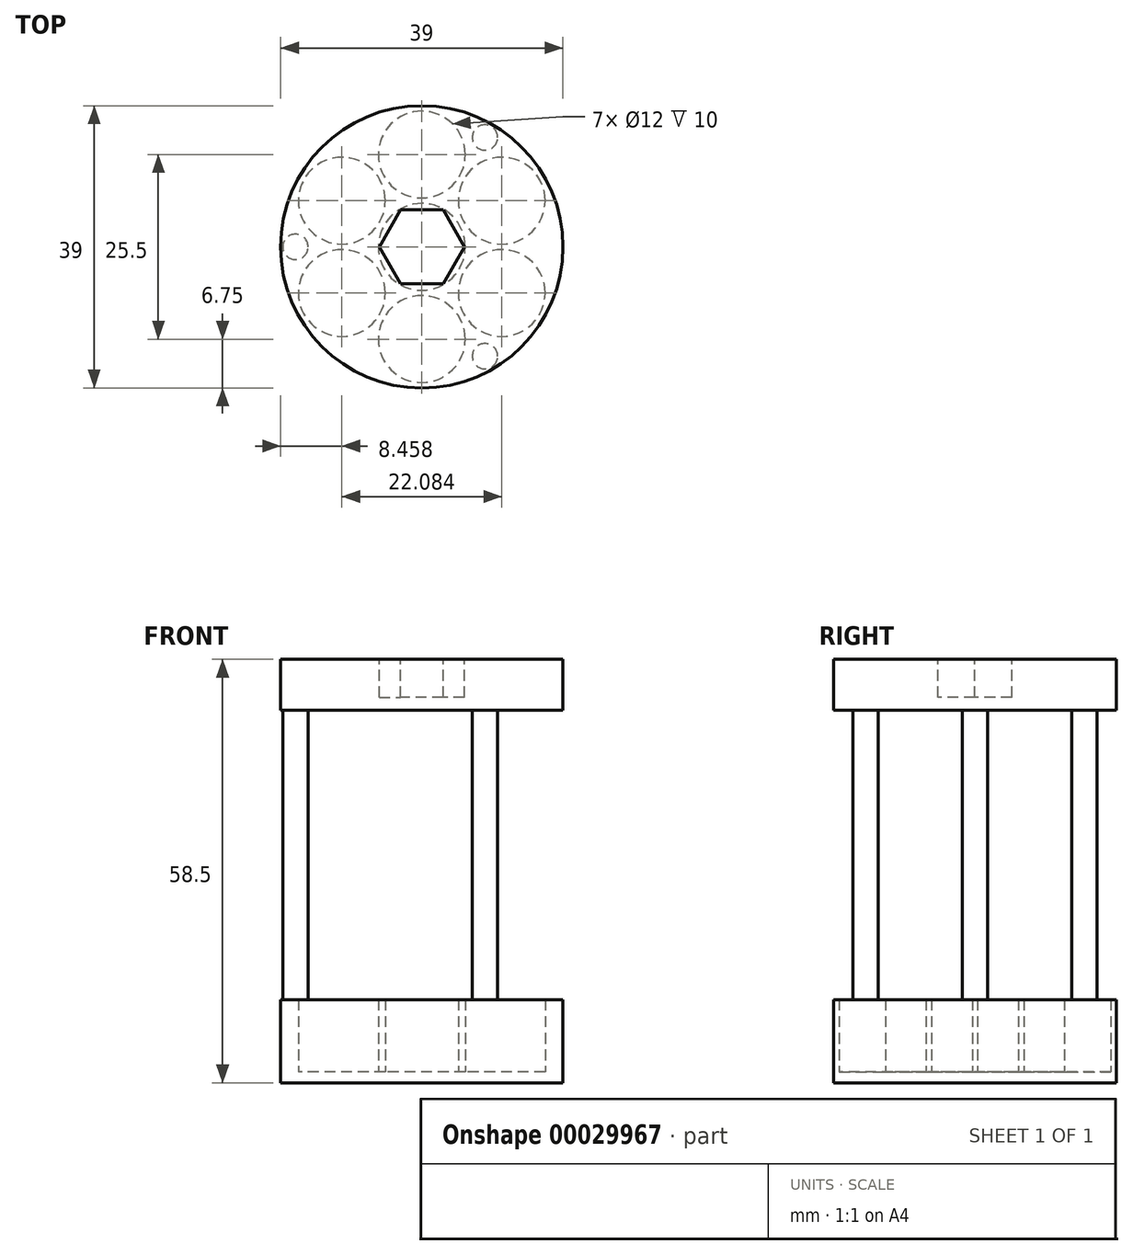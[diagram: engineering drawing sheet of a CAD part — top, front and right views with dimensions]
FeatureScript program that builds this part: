
annotation { "Feature Type Name" : "Feature", "Feature Type Description" : "" }
export const myFeature = defineFeature(function(context is Context, id is Id, definition is map)
    precondition{}
    {
        {
            var Q0;
            Q0=qCreatedBy(makeId("Top.planeOp"),FACE);
            var sketch = newSketch(context, id + "F0", { "sketchPlane" : qUnion([Q0])});
            skCircle(sketch, "E0", {"center": v(0, 0) * mm, "radius": 19.5 * mm});
            skSolve(sketch);
        }
        {
            var Q0;
            Q0=qSketchRegion(id+"F0",true);
            extrude(context, id + "F1", {"entities" : qUnion([Q0]), "depth" : 1.5 * mm});
        }
        {
            var Q0;
            Q0=makeQuery(id+"F1.opExtrude","CAP_FACE",FACE,{"disambiguationData":[OSD([sQuery(id+"F0.wireOp",EDGE,"E0")])],"isStart":false});
            var sketch = newSketch(context, id + "F2", { "sketchPlane" : qUnion([Q0])});
            skCircle(sketch, "E1", {"center": v(0, 0) * mm, "radius": 19.5 * mm});
            skCircle(sketch, "E2", {"center": v(0, 0) * mm, "radius": 6 * mm});
            skLineSegment(sketch, "E3", {"start": v(0, 6) * mm, "end": v(0, 19.5) * mm});
            skCircle(sketch, "E4", {"center": v(0, 12.75) * mm, "radius": 6 * mm});
            skCircle(sketch, "E5.1.0", {"center": v(-11.04, 6.38) * mm, "radius": 6 * mm});
            skCircle(sketch, "E5.2.0", {"center": v(-11.04, -6.37) * mm, "radius": 6 * mm});
            skCircle(sketch, "E5.3.0", {"center": v(0, -12.75) * mm, "radius": 6 * mm});
            skCircle(sketch, "E5.4.0", {"center": v(11.04, -6.38) * mm, "radius": 6 * mm});
            skCircle(sketch, "E5.5.0", {"center": v(11.04, 6.38) * mm, "radius": 6 * mm});
            skSolve(sketch);
        }
        {
            var Q0;
            Q0=makeQuery(id+"F2.imprint","IMPRINT",FACE,{"disambiguationData":[TD([[makeQuery(id+"F2.imprint","IMPRINT",EDGE,{"derivedFrom":sQuery(id+"F2.wireOp",EDGE,"E1")}),1.0]])]});
            extrude(context, id + "F3", {"entities" : qUnion([Q0]), "operationType" : NewBodyOperationType.ADD, "depth" : 10 * mm});
        }
        {
            var Q0;
            Q0=makeQuery(id+"F3.opExtrude","CAP_FACE",FACE,{"disambiguationData":[OSD([sQuery(id+"F2.wireOp",EDGE,"E1"),sQuery(id+"F2.wireOp",EDGE,"E2"),sQuery(id+"F2.wireOp",EDGE,"E4"),sQuery(id+"F2.wireOp",EDGE,"E5.1.0"),sQuery(id+"F2.wireOp",EDGE,"E5.2.0"),sQuery(id+"F2.wireOp",EDGE,"E5.3.0"),sQuery(id+"F2.wireOp",EDGE,"E5.4.0"),sQuery(id+"F2.wireOp",EDGE,"E5.5.0")])],"isStart":false});
            var sketch = newSketch(context, id + "F4", { "sketchPlane" : qUnion([Q0])});
            skCircle(sketch, "E6", {"center": v(-17.45, 0) * mm, "radius": 1.75 * mm});
            skCircle(sketch, "E7.1.0", {"center": v(8.72, -15.11) * mm, "radius": 1.75 * mm});
            skCircle(sketch, "E7.2.0", {"center": v(8.72, 15.11) * mm, "radius": 1.75 * mm});
            skPoint(sketch, "E7.center", {"position": v(0, 0) * mm});
            skSolve(sketch);
        }
        {
            var Q0;
            Q0=qSketchRegion(id+"F4",true);
            extrude(context, id + "F5", {"entities" : qUnion([Q0]), "operationType" : NewBodyOperationType.ADD, "depth" : 40 * mm});
        }
        {
            var Q0;
            Q0=makeQuery(id+"F5.opExtrude","CAP_FACE",FACE,{"disambiguationData":[OSD([sQuery(id+"F4.wireOp",EDGE,"E7.2.0")])],"isStart":false});
            var sketch = newSketch(context, id + "F6", { "sketchPlane" : qUnion([Q0])});
            skCircle(sketch, "E8", {"center": v(0, 0) * mm, "radius": 19.5 * mm});
            skSolve(sketch);
        }
        {
            var Q0;
            Q0=makeQuery(id+"F6.imprint","IMPRINT",FACE,{"disambiguationData":[TD([[makeQuery(id+"F6.imprint","IMPRINT",EDGE,{"derivedFrom":sQuery(id+"F6.wireOp",EDGE,"E8")}),1.0]])]});
            var Q1;
            Q1=makeQuery(id+"F6.imprint","IMPRINT",FACE,{"disambiguationData":[TD([[makeQuery(id+"F6.imprint","IMPRINT",EDGE,{"derivedFrom":makeQuery(id+"F5.opExtrude","CAP_EDGE",EDGE,{"disambiguationData":[OSD([sQuery(id+"F4.wireOp",EDGE,"E7.2.0")])],"isStart":false})}),1.0]])]});
            extrude(context, id + "F7", {"entities" : qUnion([Q0, Q1]), "operationType" : NewBodyOperationType.ADD, "depth" : 7 * mm});
        }
        {
            var Q0;
            Q0=makeQuery(id+"F7.opExtrude","CAP_FACE",FACE,{"disambiguationData":[OSD([sQuery(id+"F6.wireOp",EDGE,"E8")])],"isStart":false});
            var sketch = newSketch(context, id + "F8", { "sketchPlane" : qUnion([Q0])});
            skCircle(sketch, "E9.cCircle", {"center": v(0, 0) * mm, "radius": 5.1 * mm, "construction": true});
            skLineSegment(sketch, "E9.0", {"start": v(2.94, -5.1) * mm, "end": v(-2.94, -5.1) * mm});
            skLineSegment(sketch, "E9.1", {"start": v(-2.94, -5.1) * mm, "end": v(-5.89, 0) * mm});
            skLineSegment(sketch, "E9.2", {"start": v(-5.89, 0) * mm, "end": v(-2.94, 5.1) * mm});
            skLineSegment(sketch, "E9.3", {"start": v(-2.94, 5.1) * mm, "end": v(2.94, 5.1) * mm});
            skLineSegment(sketch, "E9.4", {"start": v(2.94, 5.1) * mm, "end": v(5.89, 0) * mm});
            skLineSegment(sketch, "E9.5", {"start": v(5.89, 0) * mm, "end": v(2.94, -5.1) * mm});
            skPoint(sketch, "E9.0.midPoint", {"position": v(0, -5.1) * mm});
            skSolve(sketch);
        }
        {
            var Q0;
            Q0=makeQuery(id+"F8.imprint","IMPRINT",FACE,{"disambiguationData":[TD([[makeQuery(id+"F8.imprint","IMPRINT",EDGE,{"derivedFrom":sQuery(id+"F8.wireOp",EDGE,"E9.0")}),-1.0]])]});
            extrude(context, id + "F9", {"entities" : qUnion([Q0]), "operationType" : NewBodyOperationType.REMOVE, "oppositeDirection" : true, "depth" : 5.25 * mm});
        }
    });
